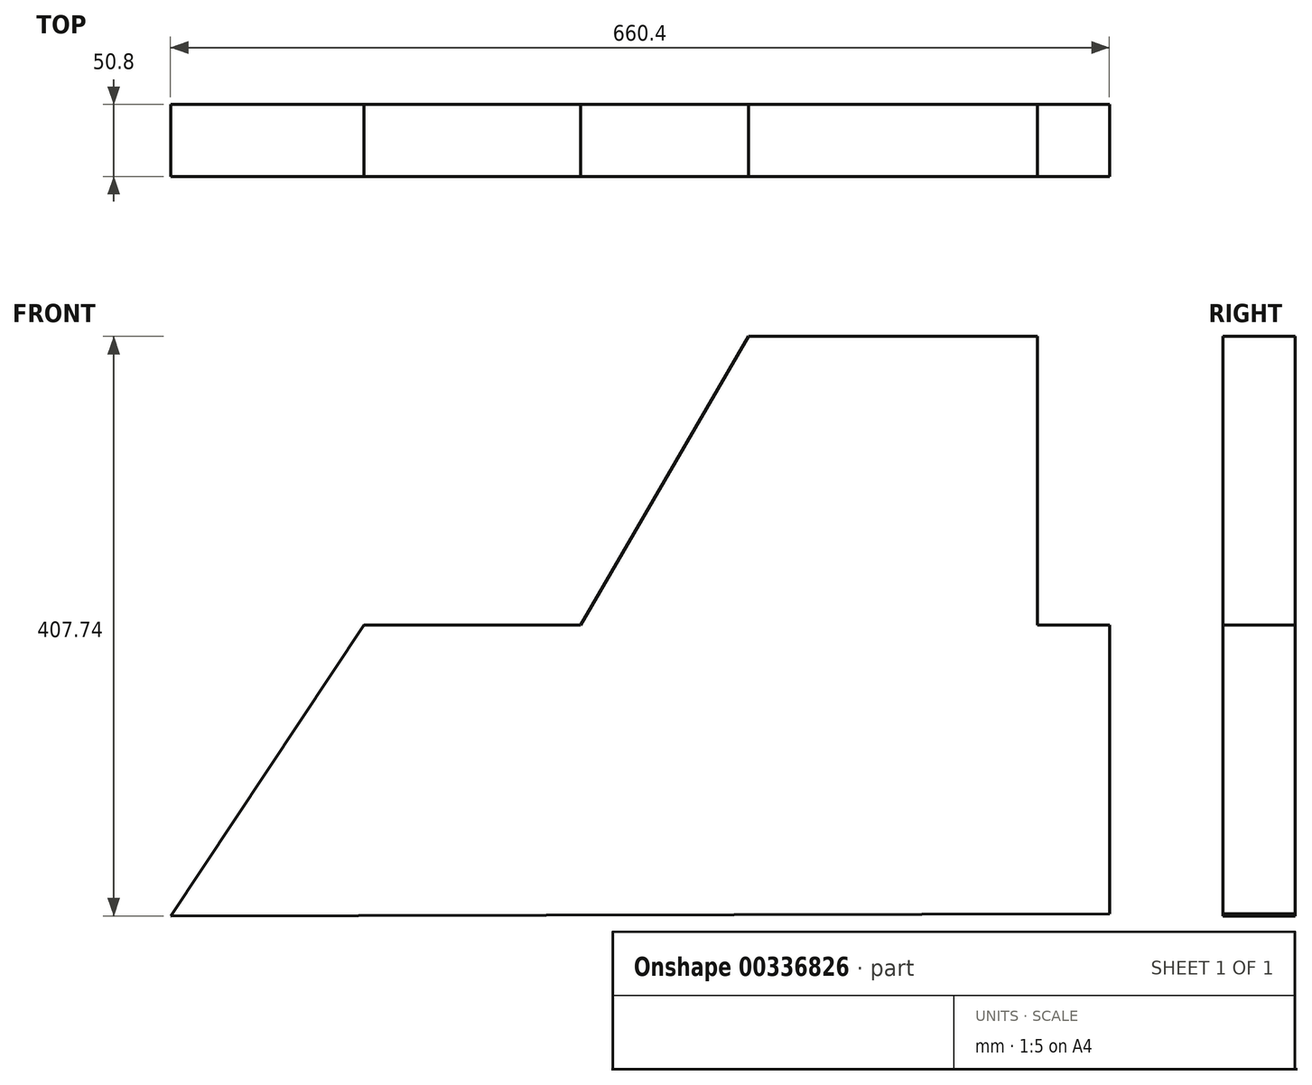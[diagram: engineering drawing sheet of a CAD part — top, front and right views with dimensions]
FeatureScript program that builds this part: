
annotation { "Feature Type Name" : "Feature", "Feature Type Description" : "" }
export const myFeature = defineFeature(function(context is Context, id is Id, definition is map)
    precondition{}
    {
        {
            var Q0;
            Q0=qCreatedBy(makeId("Front.planeOp"),FACE);
            var sketch = newSketch(context, id + "F0", { "sketchPlane" : qUnion([Q0])});
            skLineSegment(sketch, "E0", {"start": v(-316.68, -194.82) * mm, "end": v(-180.66, 9.72) * mm});
            skLineSegment(sketch, "E1", {"start": v(-180.66, 9.72) * mm, "end": v(-28.26, 9.72) * mm});
            skLineSegment(sketch, "E2", {"start": v(89.72, 212.92) * mm, "end": v(292.92, 212.92) * mm});
            skLineSegment(sketch, "E3", {"start": v(292.92, 212.92) * mm, "end": v(292.92, 9.72) * mm});
            skLineSegment(sketch, "E4", {"start": v(292.92, 9.72) * mm, "end": v(343.72, 9.72) * mm});
            skLineSegment(sketch, "E5", {"start": v(343.72, 9.72) * mm, "end": v(343.72, -193.48) * mm});
            skLineSegment(sketch, "E6", {"start": v(-316.68, -194.82) * mm, "end": v(343.72, -193.48) * mm});
            skLineSegment(sketch, "E7", {"start": v(-28.26, 9.72) * mm, "end": v(89.72, 212.92) * mm});
            skSolve(sketch);
        }
        {
            var Q0;
            Q0=makeQuery(id+"F0.imprint","IMPRINT",FACE,{"disambiguationData":[TD([[makeQuery(id+"F0.imprint","IMPRINT",EDGE,{"derivedFrom":sQuery(id+"F0.wireOp",EDGE,"E0")}),-1.0]])]});
            extrude(context, id + "F1", {"entities" : qUnion([Q0]), "depth" : 50.8 * mm});
        }
    });
